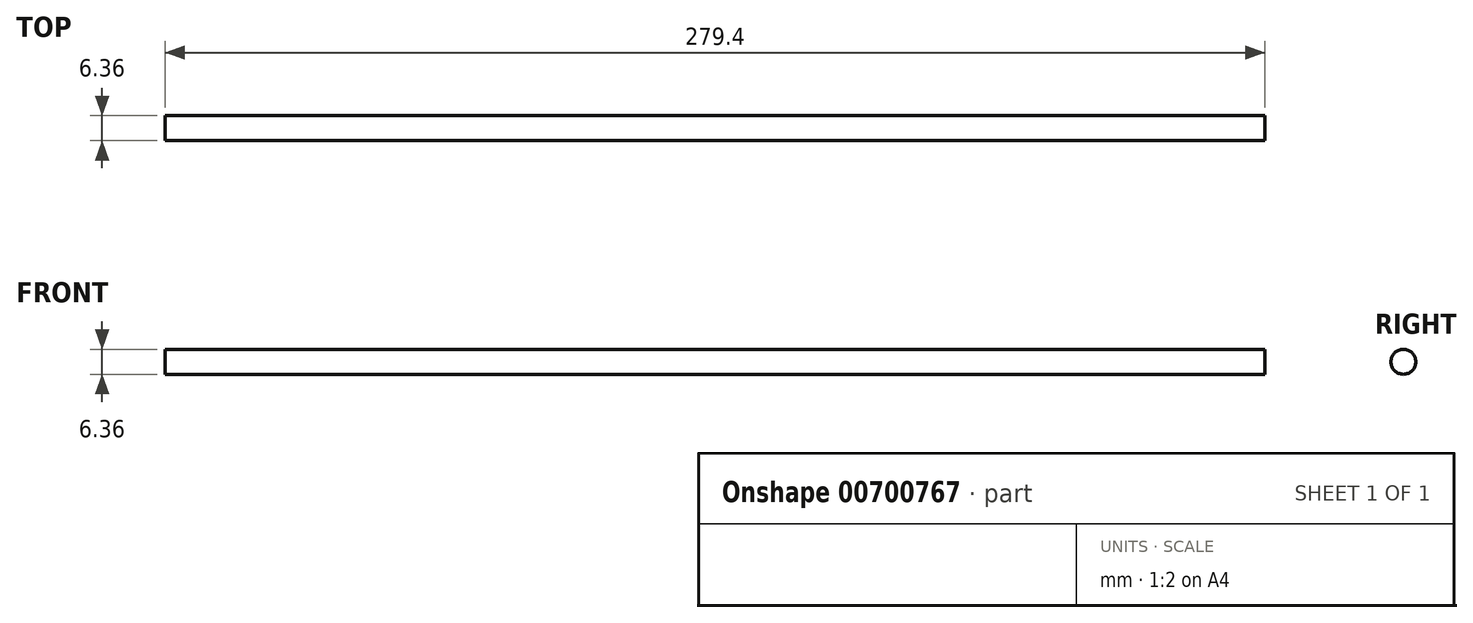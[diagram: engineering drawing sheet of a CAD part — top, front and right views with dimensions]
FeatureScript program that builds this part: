
annotation { "Feature Type Name" : "Feature", "Feature Type Description" : "" }
export const myFeature = defineFeature(function(context is Context, id is Id, definition is map)
    precondition{}
    {
        {
            var Q0;
            Q0=qCreatedBy(makeId("Right.planeOp"),FACE);
            var sketch = newSketch(context, id + "F0", { "sketchPlane" : qUnion([Q0])});
            skCircle(sketch, "E0", {"center": v(0, 0) * mm, "radius": 3.18 * mm});
            skSolve(sketch);
        }
        {
            var Q0;
            Q0 = qSketchRegion(id + "F0", true);
            extrude(context, id + "F1", {"entities" : qUnion([Q0]), "endBound" : BoundingType.SYMMETRIC, "depth" : 279.4 * mm, "offsetDistance" : 25.4 * mm});
        }
    });
